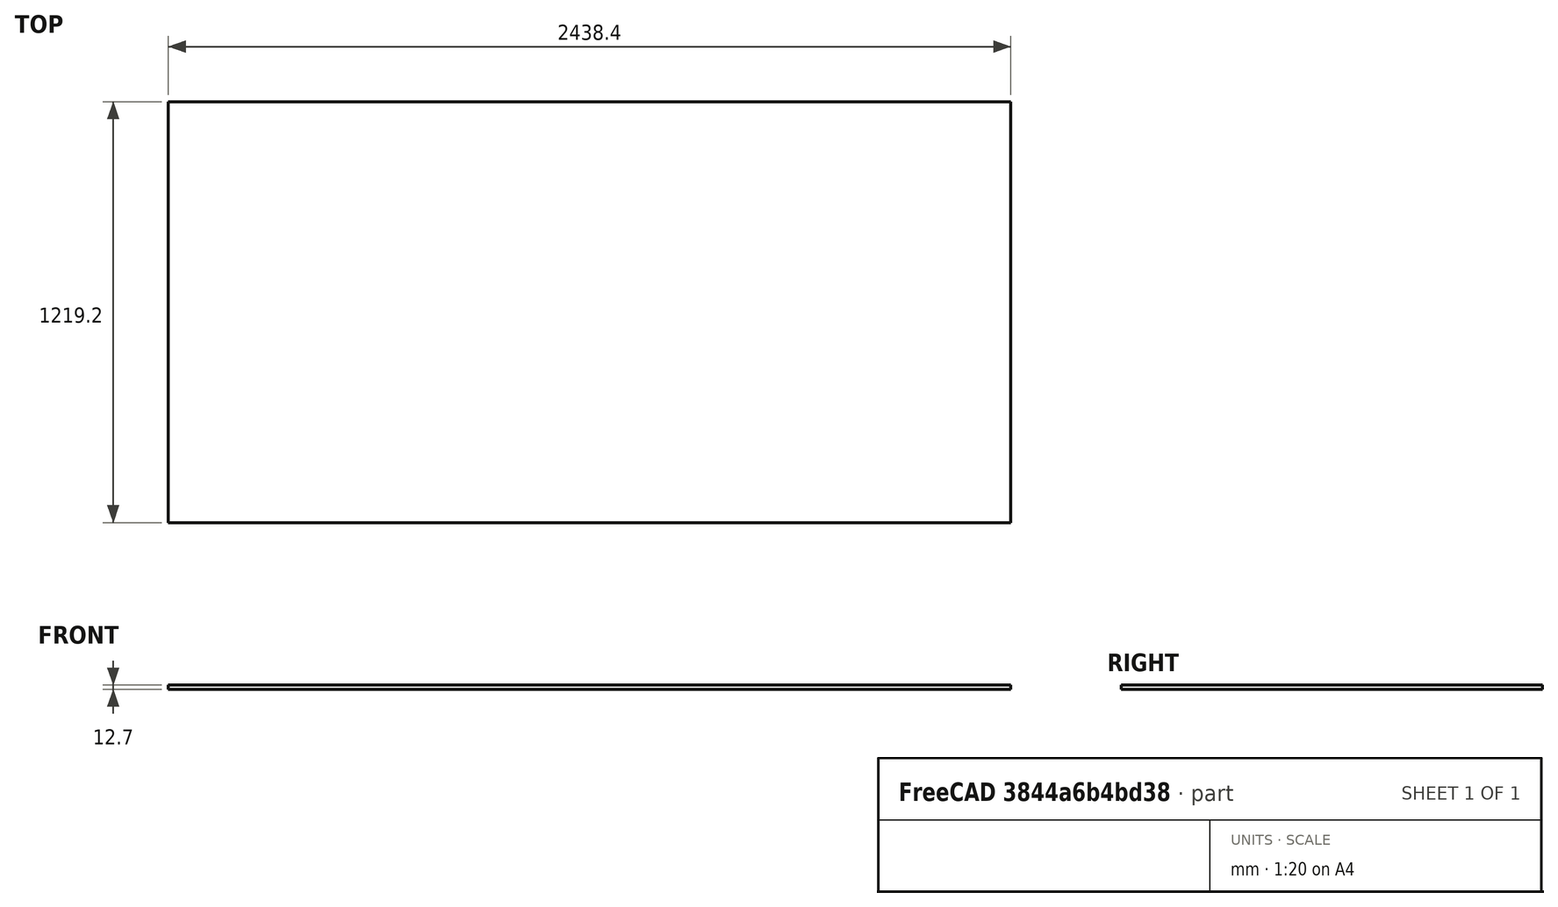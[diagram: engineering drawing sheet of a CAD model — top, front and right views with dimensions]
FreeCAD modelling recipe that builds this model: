
FCSTD DOCUMENT  (FreeCAD 0.19R24291 (Git))
Label: plywood4x8x0.5
License: All rights reserved
LicenseURL: http://en.wikipedia.org/wiki/All_rights_reserved
objects: App::AnnotationLabel×2, Sketcher::SketchObject×1, PartDesign::Pad×1, PartDesign::Body×1, App::DocumentObjectGroup×1
note: 4 computed .brp shape members not serialized (recipe doc carries the construction recipe); baked Part::Feature solids carry a one-line shape summary decoded from their .brp

FEATURE [Sketcher::SketchObject] Sketch
  FullyConstrained = true
  MapMode = 5
  Support = -> [XY_Plane]
  expr: Constraints[10] = 8 * 12 * 25.4
  expr: Constraints[9] = 4 * 12 * 25.4
  sketch-geometry (4):
    g0: LineSegment StartX=0 StartY=0 StartZ=0 EndX=2438.4 EndY=0 EndZ=0
    g1: LineSegment StartX=2438.4 StartY=0 StartZ=0 EndX=2438.4 EndY=1219.2 EndZ=0
    g2: LineSegment StartX=2438.4 StartY=1219.2 StartZ=0 EndX=0 EndY=1219.2 EndZ=0
    g3: LineSegment StartX=0 StartY=1219.2 StartZ=0 EndX=0 EndY=0 EndZ=0
  constraints (11):
    c: Coincident(g0,g1)
    c: Coincident(g1,g2)
    c: Coincident(g2,g3)
    c: Coincident(g3,g0)
    c: Horizontal(g0)
    c: Horizontal(g2)
    c: Vertical(g1)
    c: Vertical(g3)
    c: Coincident(g0,g-1)
    c: DistanceY(g3,g3) = 1219.2
    c: DistanceX(g0,g0) = 2438.4
FEATURE [PartDesign::Pad] Pad
  Direction = (1,1,1)
  Length = 12.7
  Length2 = 100
  Profile = -> Sketch
  Type = 0
  expr: Length = 0.5 * 25.4
FEATURE [PartDesign::Body] Body
  Group = -> [Sketch,Pad]
  Origin = -> Origin
  Tip = -> Pad
FEATURE [App::AnnotationLabel] dofLabel
  BasePosition = (1219.2,609.6,6.35)
  LabelText = FREE
  TextPosition = (0,0,0)
FEATURE [App::AnnotationLabel] dofLabel001
  BasePosition = (1219.2,609.6,6.35)
  LabelText = FREE
  TextPosition = (0,0,0)
FEATURE [App::DocumentObjectGroup] dofLabels
  Group = -> [dofLabel,dofLabel001]
